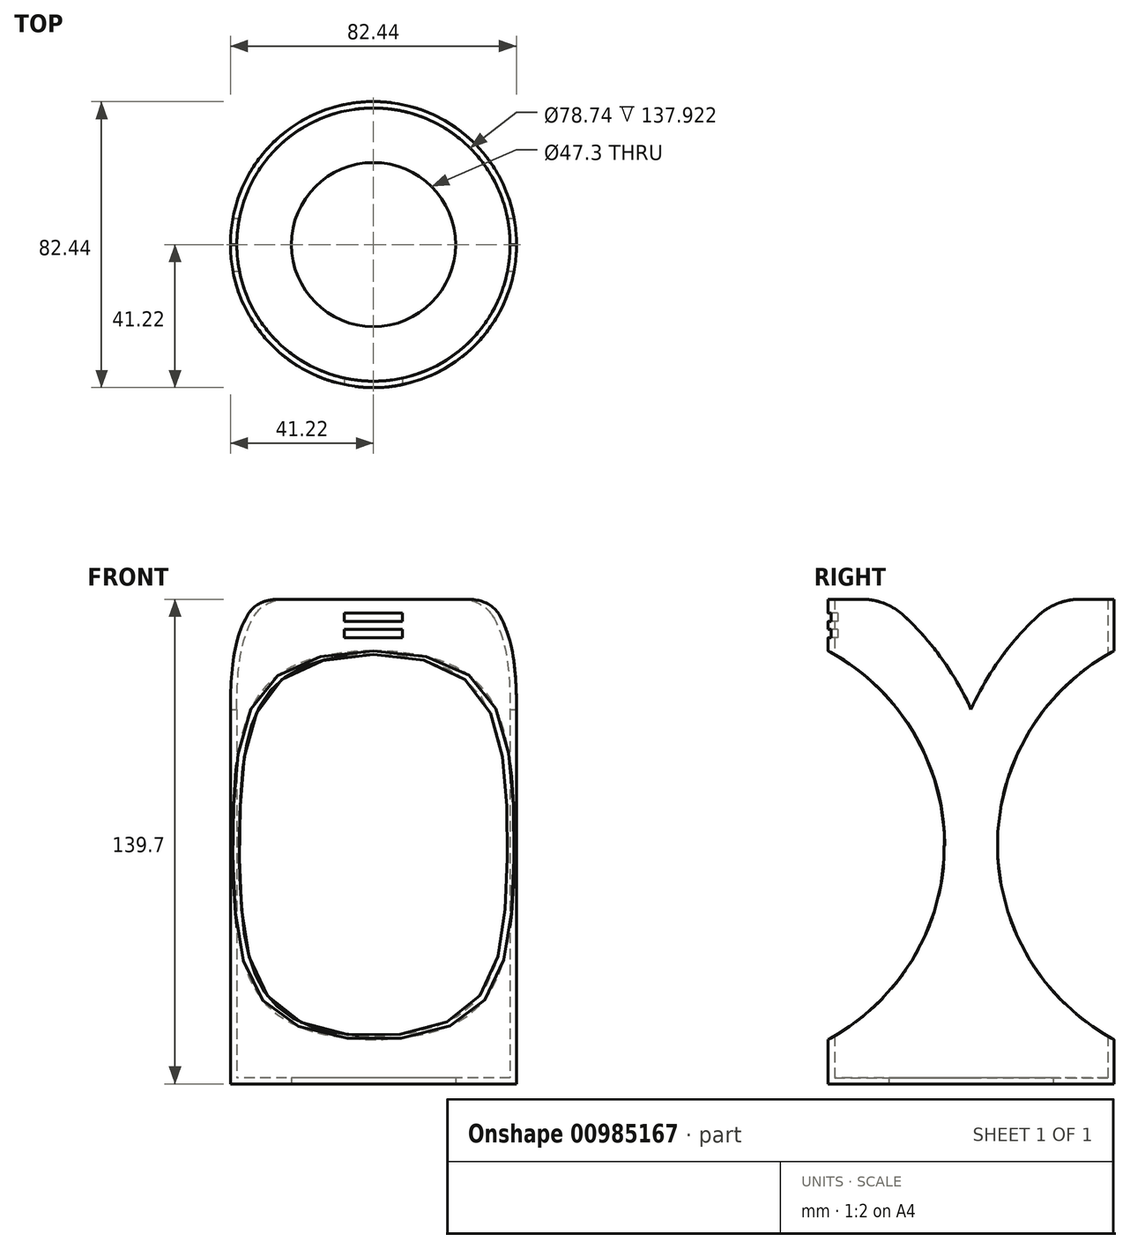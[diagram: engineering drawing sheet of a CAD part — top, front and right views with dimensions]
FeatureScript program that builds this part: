
annotation { "Feature Type Name" : "Feature", "Feature Type Description" : "" }
export const myFeature = defineFeature(function(context is Context, id is Id, definition is map)
    precondition{}
    {
        {
            var Q0;
            Q0=qCreatedBy(makeId("Top.planeOp"),FACE);
            var sketch = newSketch(context, id + "F0", { "sketchPlane" : qUnion([Q0])});
            skCircle(sketch, "E0", {"center": v(0, 0) * mm, "radius": 39.37 * mm});
            skSolve(sketch);
        }
        {
            var Q0;
            Q0=makeQuery(id+"F0.imprint","IMPRINT",FACE,{"disambiguationData":[TD([[makeQuery(id+"F0.imprint","IMPRINT",EDGE,{"derivedFrom":sQuery(id+"F0.wireOp",EDGE,"E0")}),1.0]])]});
            extrude(context, id + "F1", {"entities" : qUnion([Q0]), "depth" : 1.78 * mm, "offsetDistance" : 25.4 * mm});
        }
        {
            var Q0;
            Q0=makeQuery(id+"F0.imprint","IMPRINT",FACE,{"disambiguationData":[TD([[makeQuery(id+"F0.imprint","IMPRINT",EDGE,{"derivedFrom":sQuery(id+"F0.wireOp",EDGE,"E0")}),1.0]])]});
            var sketch = newSketch(context, id + "F2", { "sketchPlane" : qUnion([Q0])});
            skCircle(sketch, "E1", {"center": v(0, 0) * mm, "radius": 40.35 * mm});
            skSolve(sketch);
        }
        {
            var Q0;
            Q0 = qSketchRegion(id + "F2", true);
            extrude(context, id + "F3", {"entities" : qUnion([Q0]), "operationType" : NewBodyOperationType.ADD, "depth" : 1.78 * mm, "offsetDistance" : 25.4 * mm});
        }
        {
            var Q0;
            Q0=makeQuery(id+"F0.imprint","IMPRINT",FACE,{"disambiguationData":[TD([[makeQuery(id+"F0.imprint","IMPRINT",EDGE,{"derivedFrom":sQuery(id+"F0.wireOp",EDGE,"E0")}),1.0]])]});
            var sketch = newSketch(context, id + "F4", { "sketchPlane" : qUnion([Q0])});
            skCircle(sketch, "E2", {"center": v(0, 0) * mm, "radius": 23.65 * mm});
            skSolve(sketch);
        }
        {
            var Q0;
            Q0 = qSketchRegion(id + "F4", true);
            extrude(context, id + "F5", {"entities" : qUnion([Q0]), "operationType" : NewBodyOperationType.REMOVE, "depth" : 25.4 * mm, "offsetDistance" : 25.4 * mm});
        }
        {
            var Q0;
            Q0=makeQuery(id+"F0.imprint","IMPRINT",FACE,{"disambiguationData":[TD([[makeQuery(id+"F0.imprint","IMPRINT",EDGE,{"derivedFrom":sQuery(id+"F0.wireOp",EDGE,"E0")}),1.0]])]});
            var sketch = newSketch(context, id + "F6", { "sketchPlane" : qUnion([Q0])});
            skCircle(sketch, "E3", {"center": v(0, 0) * mm, "radius": 39.37 * mm});
            skCircle(sketch, "E4", {"center": v(0, 0) * mm, "radius": 41.22 * mm});
            skSolve(sketch);
        }
        {
            var Q0;
            Q0 = qSketchRegion(id + "F6", true);
            extrude(context, id + "F7", {"entities" : qUnion([Q0]), "operationType" : NewBodyOperationType.ADD, "depth" : 139.7 * mm, "offsetDistance" : 25.4 * mm});
        }
        {
            var Q0;
            Q0=qCreatedBy(makeId("Right.planeOp"),FACE);
            cPlane(context, id + "F8", {"entities" : qUnion([Q0]), "cplaneType" : CPlaneType.OFFSET, "offset" : 152.4 * mm, "width" : 152.4 * mm, "height" : 152.4 * mm});
        }
        {
            var Q0;
            Q0=qCreatedBy(id+"F8.planeOp",FACE);
            var sketch = newSketch(context, id + "F9", { "sketchPlane" : qUnion([Q0])});
            skLineSegment(sketch, "E5", {"start": v(0, -30.82) * mm, "end": v(0, 140.05) * mm});
            skLineSegment(sketch, "E6", {"start": v(0, 68.8) * mm, "end": v(71.12, 68.8) * mm});
            skLineSegment(sketch, "E7", {"start": v(0, 68.8) * mm, "end": v(-71.12, 68.8) * mm});
            skCircle(sketch, "E8", {"center": v(71.12, 68.8) * mm, "radius": 63.5 * mm});
            skCircle(sketch, "E9", {"center": v(-71.12, 68.8) * mm, "radius": 63.5 * mm});
            skLineSegment(sketch, "E10", {"start": v(0, 140.05) * mm, "end": v(25.4, 140.05) * mm});
            skLineSegment(sketch, "E11", {"start": v(0, 140.05) * mm, "end": v(-25.4, 140.05) * mm});
            skArc(sketch, "E12", {"start": v(0, 107.95) * mm, "mid": v(-10.7, 125.58) * mm, "end": v(-25.4, 140.05) * mm});
            skArc(sketch, "E13", {"start": v(25.4, 140.05) * mm, "mid": v(10.7, 125.58) * mm, "end": v(0, 107.95) * mm});
            skSolve(sketch);
        }
        {
            var Q0;
            Q0 = qSketchRegion(id + "F9", true);
            extrude(context, id + "F10", {"entities" : qUnion([Q0]), "operationType" : NewBodyOperationType.REMOVE, "endBound" : BoundingType.THROUGH_ALL, "oppositeDirection" : true, "depth" : 25.4 * mm, "offsetDistance" : 25.4 * mm});
        }
        {
            var Q0;
            Q0=qCreatedBy(makeId("Front.planeOp"),FACE);
            cPlane(context, id + "F11", {"entities" : qUnion([Q0]), "cplaneType" : CPlaneType.OFFSET, "offset" : 76.2 * mm, "width" : 152.4 * mm, "height" : 152.4 * mm});
        }
        {
            var Q0;
            Q0=qCreatedBy(id+"F11.planeOp",FACE);
            var sketch = newSketch(context, id + "F12", { "sketchPlane" : qUnion([Q0])});
            skLineSegment(sketch, "E14", {"start": v(0, -11.49) * mm, "end": v(0, 128.56) * mm});
            skLineSegment(sketch, "E15", {"start": v(0, 128.56) * mm, "end": v(8.38, 128.56) * mm});
            skLineSegment(sketch, "E16", {"start": v(8.38, 128.56) * mm, "end": v(8.38, 131.02) * mm});
            skLineSegment(sketch, "E17", {"start": v(0, 128.56) * mm, "end": v(-8.38, 128.56) * mm});
            skLineSegment(sketch, "E18", {"start": v(8.38, 131.02) * mm, "end": v(-8.38, 131.02) * mm});
            skLineSegment(sketch, "E19", {"start": v(-8.38, 131.02) * mm, "end": v(-8.38, 128.56) * mm});
            skLineSegment(sketch, "E20", {"start": v(8.38, 133.3) * mm, "end": v(-8.38, 133.3) * mm});
            skLineSegment(sketch, "E21", {"start": v(-8.38, 133.3) * mm, "end": v(-8.38, 135.75) * mm});
            skLineSegment(sketch, "E22", {"start": v(-8.38, 135.75) * mm, "end": v(8.38, 135.75) * mm});
            skLineSegment(sketch, "E23", {"start": v(8.38, 135.75) * mm, "end": v(8.38, 133.3) * mm});
            skSolve(sketch);
        }
        {
            var Q0;
            Q0 = qSketchRegion(id + "F12", true);
            extrude(context, id + "F13", {"entities" : qUnion([Q0]), "operationType" : NewBodyOperationType.REMOVE, "oppositeDirection" : true, "depth" : 101.6 * mm, "offsetDistance" : 25.4 * mm});
        }
        {
            var Q0;
            Q0=makeQuery(id+"F10.boolean.opBoolean","INTERSECT",EDGE,{"disambiguationData":[OD(1.0)],"derivedFrom":[makeQuery(id+"F7.opExtrude","CAP_FACE",FACE,{"disambiguationData":[OSD([sQuery(id+"F6.wireOp",EDGE,"E3"),sQuery(id+"F6.wireOp",EDGE,"E4")])],"isStart":false}),makeQuery(id+"F10.opExtrude","SWEPT_FACE",FACE,{"disambiguationData":[OSD([sQuery(id+"F9.wireOp",EDGE,"E12")])]})]});
            var Q1;
            Q1=makeQuery(id+"F10.boolean.opBoolean","INTERSECT",EDGE,{"disambiguationData":[OD(1.0)],"derivedFrom":[makeQuery(id+"F7.opExtrude","CAP_FACE",FACE,{"disambiguationData":[OSD([sQuery(id+"F6.wireOp",EDGE,"E3"),sQuery(id+"F6.wireOp",EDGE,"E4")])],"isStart":false}),makeQuery(id+"F10.opExtrude","SWEPT_FACE",FACE,{"disambiguationData":[OSD([sQuery(id+"F9.wireOp",EDGE,"E13")])]})]});
            var Q2;
            Q2=makeQuery(id+"F10.boolean.opBoolean","INTERSECT",EDGE,{"disambiguationData":[OD(0.0)],"derivedFrom":[makeQuery(id+"F7.opExtrude","CAP_FACE",FACE,{"disambiguationData":[OSD([sQuery(id+"F6.wireOp",EDGE,"E3"),sQuery(id+"F6.wireOp",EDGE,"E4")])],"isStart":false}),makeQuery(id+"F10.opExtrude","SWEPT_FACE",FACE,{"disambiguationData":[OSD([sQuery(id+"F9.wireOp",EDGE,"E12")])]})]});
            var Q3;
            Q3=makeQuery(id+"F10.boolean.opBoolean","INTERSECT",EDGE,{"disambiguationData":[OD(0.0)],"derivedFrom":[makeQuery(id+"F7.opExtrude","CAP_FACE",FACE,{"disambiguationData":[OSD([sQuery(id+"F6.wireOp",EDGE,"E3"),sQuery(id+"F6.wireOp",EDGE,"E4")])],"isStart":false}),makeQuery(id+"F10.opExtrude","SWEPT_FACE",FACE,{"disambiguationData":[OSD([sQuery(id+"F9.wireOp",EDGE,"E13")])]})]});
            fillet(context, id + "F14", {"entities" : qUnion([Q0, Q1, Q2, Q3]), "radius" : 17.78 * mm, "tangentPropagation" : true, "allowEdgeOverflow" : false});
        }
    });
